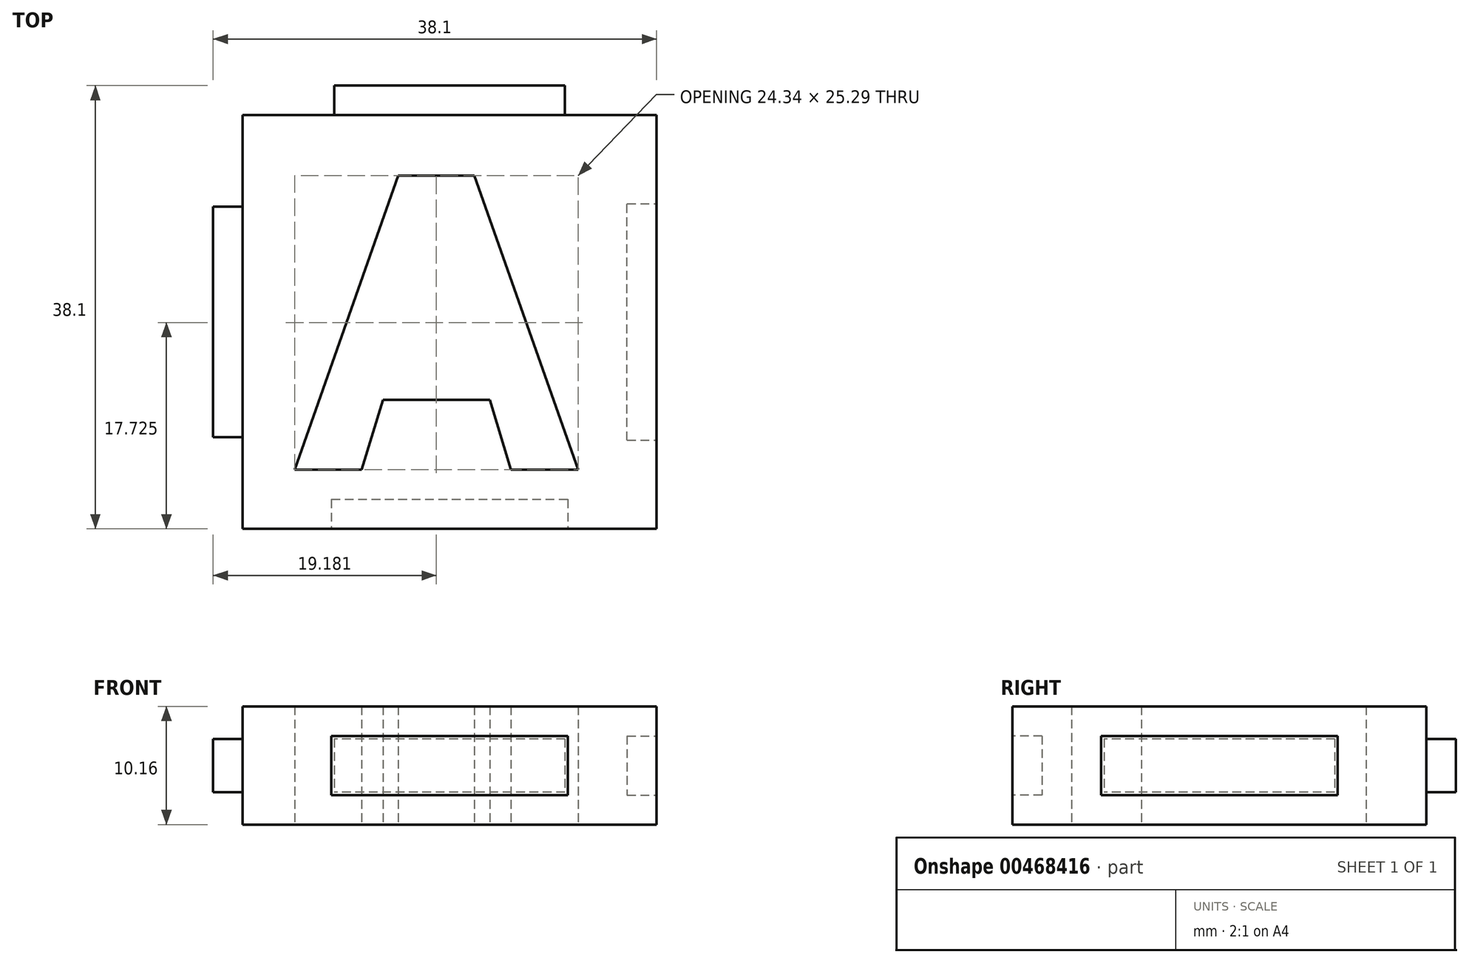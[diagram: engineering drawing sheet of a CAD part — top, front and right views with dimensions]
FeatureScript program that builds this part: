
annotation { "Feature Type Name" : "Feature", "Feature Type Description" : "" }
export const myFeature = defineFeature(function(context is Context, id is Id, definition is map)
    precondition{}
    {
        {
            var Q0;
            Q0=qCreatedBy(makeId("Top.planeOp"),FACE);
            var sketch = newSketch(context, id + "F0", { "sketchPlane" : qUnion([Q0])});
            skText(sketch, "E0", { "text": "A", "fontName": "OpenSans-Bold.ttf"});
            skLineSegment(sketch, "E1.bottom", {"start": v(-17.78, 17.78) * mm, "end": v(17.78, 17.78) * mm});
            skLineSegment(sketch, "E1.top", {"start": v(-17.78, -17.78) * mm, "end": v(17.78, -17.78) * mm});
            skLineSegment(sketch, "E1.left", {"start": v(-17.78, 17.78) * mm, "end": v(-17.78, -17.78) * mm});
            skLineSegment(sketch, "E1.right", {"start": v(17.78, 17.78) * mm, "end": v(17.78, -17.78) * mm});
            const initialGuessF0  = {"E0": [-0.01331, -0.0127, 1, 0, 0.0254]};
            skSetInitialGuess(sketch, initialGuessF0);
            skSolve(sketch);
        }
        {
            var Q0;
            Q0 = qSketchRegion(id + "F0", true);
            extrude(context, id + "F1", {"entities" : qUnion([Q0]), "endBound" : BoundingType.SYMMETRIC, "depth" : 10.16 * mm});
        }
        {
            var Q0;
            Q0=makeQuery(id+"F1.opExtrude","SWEPT_FACE",FACE,{"disambiguationData":[OSD([sQuery(id+"F0.wireOp",EDGE,"E1.bottom")])]});
            var sketch = newSketch(context, id + "F2", { "sketchPlane" : qUnion([Q0])});
            skLineSegment(sketch, "E2.bottom", {"start": v(-9.9, 2.29) * mm, "end": v(9.9, 2.29) * mm});
            skLineSegment(sketch, "E2.top", {"start": v(-9.9, -2.29) * mm, "end": v(9.9, -2.29) * mm});
            skLineSegment(sketch, "E2.left", {"start": v(-9.9, 2.29) * mm, "end": v(-9.9, -2.29) * mm});
            skLineSegment(sketch, "E2.right", {"start": v(9.9, 2.29) * mm, "end": v(9.9, -2.29) * mm});
            skSolve(sketch);
        }
        {
            var Q0;
            Q0 = qSketchRegion(id + "F2", true);
            extrude(context, id + "F3", {"entities" : qUnion([Q0]), "operationType" : NewBodyOperationType.ADD, "depth" : 2.54 * mm});
        }
        {
            var Q0;
            Q0=makeQuery(id+"F1.opExtrude","SWEPT_FACE",FACE,{"disambiguationData":[OSD([sQuery(id+"F0.wireOp",EDGE,"E1.left")])]});
            var sketch = newSketch(context, id + "F4", { "sketchPlane" : qUnion([Q0])});
            skLineSegment(sketch, "E3.bottom", {"start": v(-9.9, 2.29) * mm, "end": v(9.9, 2.29) * mm});
            skLineSegment(sketch, "E3.top", {"start": v(-9.9, -2.29) * mm, "end": v(9.9, -2.29) * mm});
            skLineSegment(sketch, "E3.left", {"start": v(-9.9, 2.29) * mm, "end": v(-9.9, -2.29) * mm});
            skLineSegment(sketch, "E3.right", {"start": v(9.9, 2.29) * mm, "end": v(9.9, -2.29) * mm});
            skSolve(sketch);
        }
        {
            var Q0;
            Q0 = qSketchRegion(id + "F4", true);
            extrude(context, id + "F5", {"entities" : qUnion([Q0]), "operationType" : NewBodyOperationType.ADD, "depth" : 2.54 * mm});
        }
        {
            var Q0;
            Q0=makeQuery(id+"F1.opExtrude","SWEPT_FACE",FACE,{"disambiguationData":[OSD([sQuery(id+"F0.wireOp",EDGE,"E1.top")])]});
            var sketch = newSketch(context, id + "F6", { "sketchPlane" : qUnion([Q0])});
            skLineSegment(sketch, "E4.bottom", {"start": v(-10.16, 2.54) * mm, "end": v(10.16, 2.54) * mm});
            skLineSegment(sketch, "E4.top", {"start": v(-10.16, -2.54) * mm, "end": v(10.16, -2.54) * mm});
            skLineSegment(sketch, "E4.left", {"start": v(-10.16, 2.54) * mm, "end": v(-10.16, -2.54) * mm});
            skLineSegment(sketch, "E4.right", {"start": v(10.16, 2.54) * mm, "end": v(10.16, -2.54) * mm});
            skSolve(sketch);
        }
        {
            var Q0;
            Q0 = qSketchRegion(id + "F6", true);
            extrude(context, id + "F7", {"entities" : qUnion([Q0]), "operationType" : NewBodyOperationType.REMOVE, "oppositeDirection" : true, "depth" : 2.54 * mm});
        }
        {
            var Q0;
            Q0=makeQuery(id+"F1.opExtrude","SWEPT_FACE",FACE,{"disambiguationData":[OSD([sQuery(id+"F0.wireOp",EDGE,"E1.right")])]});
            var sketch = newSketch(context, id + "F8", { "sketchPlane" : qUnion([Q0])});
            skLineSegment(sketch, "E5.bottom", {"start": v(-10.16, 2.54) * mm, "end": v(10.16, 2.54) * mm});
            skLineSegment(sketch, "E5.top", {"start": v(-10.16, -2.54) * mm, "end": v(10.16, -2.54) * mm});
            skLineSegment(sketch, "E5.left", {"start": v(-10.16, 2.54) * mm, "end": v(-10.16, -2.54) * mm});
            skLineSegment(sketch, "E5.right", {"start": v(10.16, 2.54) * mm, "end": v(10.16, -2.54) * mm});
            skSolve(sketch);
        }
        {
            var Q0;
            Q0 = qSketchRegion(id + "F8", true);
            extrude(context, id + "F9", {"entities" : qUnion([Q0]), "operationType" : NewBodyOperationType.REMOVE, "oppositeDirection" : true, "depth" : 2.54 * mm});
        }
    });
